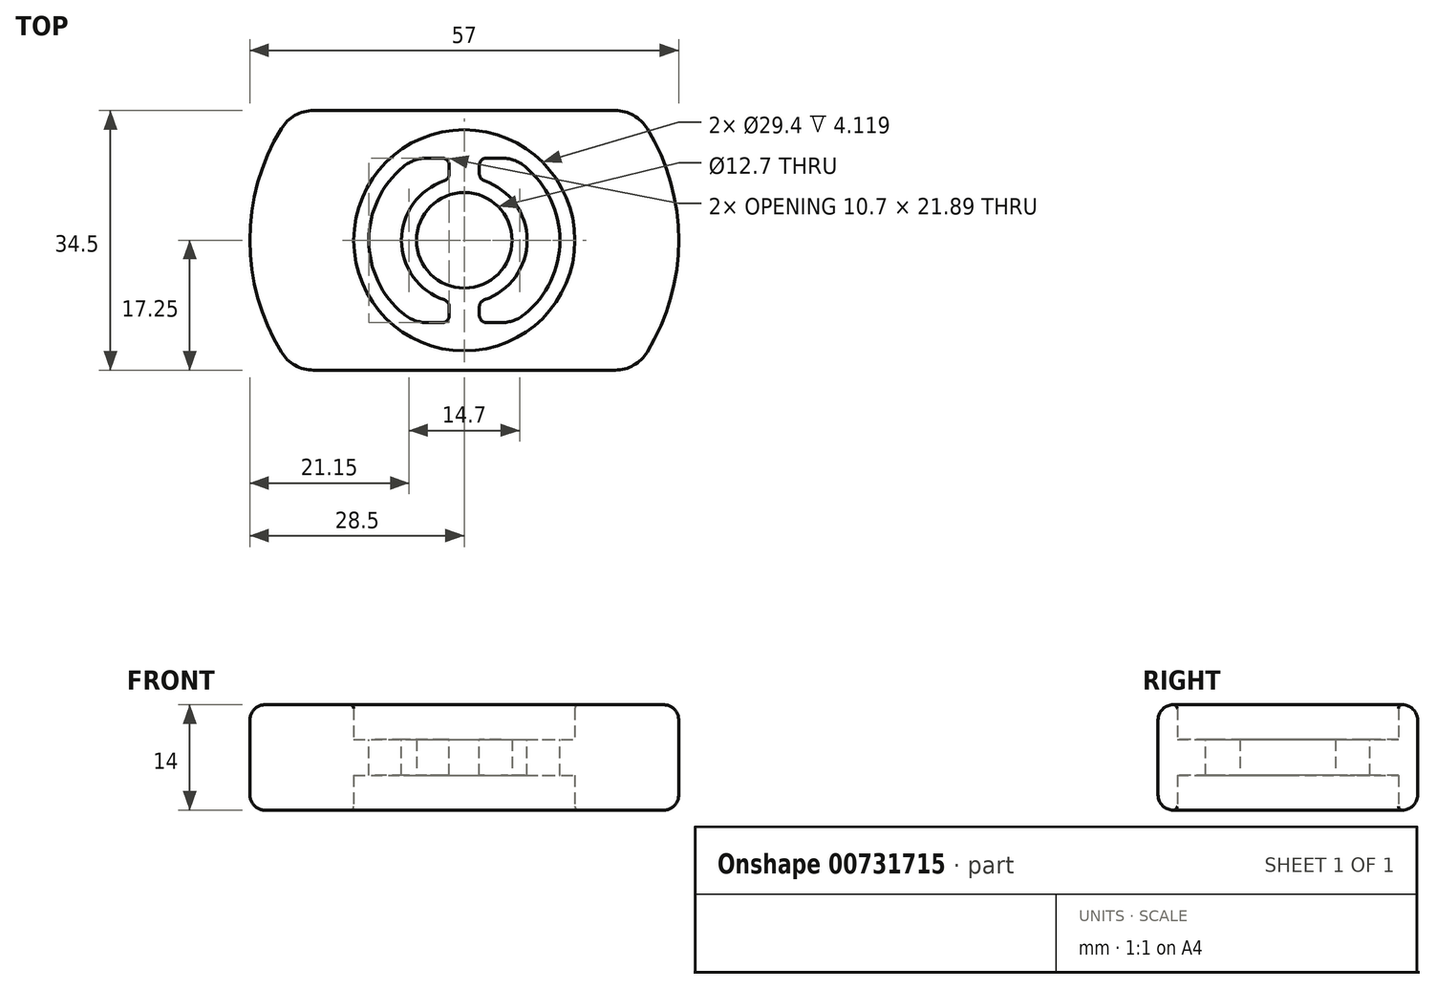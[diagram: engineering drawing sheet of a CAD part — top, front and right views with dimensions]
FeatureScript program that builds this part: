
annotation { "Feature Type Name" : "Feature", "Feature Type Description" : "" }
export const myFeature = defineFeature(function(context is Context, id is Id, definition is map)
    precondition{}
    {
        {
            var Q0;
            Q0=qCreatedBy(makeId("Front.planeOp"),FACE);
            var sketch = newSketch(context, id + "F0", { "sketchPlane" : qUnion([Q0])});
            skLineSegment(sketch, "E0", {"start": v(6.35, 0) * mm, "end": v(6.35, 4.76) * mm});
            skLineSegment(sketch, "E1", {"start": v(0, 6.26) * mm, "end": v(0, 11.13) * mm});
            skLineSegment(sketch, "E2", {"start": v(0, 19.9) * mm, "end": v(12.7, 19.9) * mm});
            skLineSegment(sketch, "E3", {"start": v(6.35, 4.76) * mm, "end": v(12.7, 4.76) * mm});
            skLineSegment(sketch, "E4", {"start": v(6.35, 0) * mm, "end": v(12.7, 0) * mm});
            skLineSegment(sketch, "E5", {"start": v(12.7, 4.76) * mm, "end": v(14.7, 4.76) * mm});
            skLineSegment(sketch, "E6", {"start": v(12.7, 0) * mm, "end": v(14.7, 0) * mm});
            skLineSegment(sketch, "E7", {"start": v(14.7, 4.76) * mm, "end": v(14.7, 6.26) * mm});
            skLineSegment(sketch, "E8", {"start": v(14.7, 0) * mm, "end": v(14.7, -1.5) * mm});
            skLineSegment(sketch, "E9", {"start": v(28.5, 2.38) * mm, "end": v(28.5, -4.62) * mm});
            skLineSegment(sketch, "E10", {"start": v(29.18, -4.62) * mm, "end": v(28.5, -4.62) * mm});
            skPoint(sketch, "E11.start.orphan", {"position": v(29.18, 11.38) * mm});
            skLineSegment(sketch, "E12", {"start": v(28.5, -4.62) * mm, "end": v(24.5, -4.62) * mm});
            skPoint(sketch, "E13.orphan", {"position": v(28.5, 13.95) * mm});
            skLineSegment(sketch, "E14", {"start": v(8.65, 12.63) * mm, "end": v(7.14, 12.63) * mm});
            skLineSegment(sketch, "E15", {"start": v(12.7, 6.26) * mm, "end": v(12.7, 6.26) * mm});
            skPoint(sketch, "E16.orphan", {"position": v(0, 12.63) * mm});
            skLineSegment(sketch, "E17", {"start": v(0, 0) * mm, "end": v(0, 4.76) * mm});
            skPoint(sketch, "E18.start.orphan", {"position": v(6.35, 2.38) * mm});
            skLineSegment(sketch, "E19", {"start": v(28.5, 2.38) * mm, "end": v(28.5, 9.38) * mm});
            skLineSegment(sketch, "E20", {"start": v(28.5, 9.38) * mm, "end": v(24.5, 9.38) * mm});
            skPoint(sketch, "E21.end.orphan", {"position": v(24.5, 11.13) * mm});
            skPoint(sketch, "E22.start.orphan", {"position": v(25.51, 2.38) * mm});
            skLineSegment(sketch, "E23", {"start": v(0, 4.76) * mm, "end": v(0, 6.26) * mm});
            skPoint(sketch, "E24.startSnap0", {"position": v(0, 5.51) * mm});
            skLineSegment(sketch, "E25", {"start": v(8.65, 10.26) * mm, "end": v(7.14, 10.26) * mm});
            skPoint(sketch, "E26.orphan", {"position": v(8.65, 11.13) * mm});
            skPoint(sketch, "E27.start.orphan", {"position": v(8.65, 9.38) * mm});
            skLineSegment(sketch, "E28", {"start": v(12.7, 5.51) * mm, "end": v(0, 5.51) * mm});
            skLineSegment(sketch, "E29", {"start": v(12.7, 5.51) * mm, "end": v(13.7, 5.51) * mm});
            skPoint(sketch, "E29.endSnap0", {"position": v(13.7, 4.76) * mm});
            skLineSegment(sketch, "E30", {"start": v(13.7, 5.51) * mm, "end": v(13.7, 6.26) * mm});
            skLineSegment(sketch, "E31", {"start": v(4.54, 2.38) * mm, "end": v(2.3, 2.38) * mm});
            skLineSegment(sketch, "E32.MirrorCS", {"start": v(12.7, -0.75) * mm, "end": v(0, -0.75) * mm});
            skLineSegment(sketch, "E33", {"start": v(13.7, -1.5) * mm, "end": v(13.7, -0.75) * mm});
            skLineSegment(sketch, "E34", {"start": v(13.7, -0.75) * mm, "end": v(12.7, -0.75) * mm});
            skLineSegment(sketch, "E35", {"start": v(0, -3.93) * mm, "end": v(0, -0.75) * mm});
            skLineSegment(sketch, "E36", {"start": v(14.7, -1.5) * mm, "end": v(14.7, -4.62) * mm});
            skLineSegment(sketch, "E37", {"start": v(14.7, -4.62) * mm, "end": v(24.5, -4.62) * mm});
            skLineSegment(sketch, "E38", {"start": v(24.5, 9.38) * mm, "end": v(14.7, 9.38) * mm});
            skLineSegment(sketch, "E39", {"start": v(14.7, 9.38) * mm, "end": v(14.7, 6.26) * mm});
            skPoint(sketch, "E40.start.orphan", {"position": v(0, 8.7) * mm});
            skLineSegment(sketch, "E41", {"start": v(13.7, 6.26) * mm, "end": v(13.7, 10.26) * mm});
            skLineSegment(sketch, "E42", {"start": v(13.7, 10.26) * mm, "end": v(8.65, 10.26) * mm});
            skPoint(sketch, "E43.MirrorCS.end.orphan", {"position": v(7.14, -5.5) * mm});
            skPoint(sketch, "E43.MirrorCS.start.orphan", {"position": v(0, -3.93) * mm});
            skPoint(sketch, "E44.end.orphan", {"position": v(8.65, -5.5) * mm});
            skLineSegment(sketch, "E45", {"start": v(13.7, -1.5) * mm, "end": v(13.7, -5.5) * mm});
            skLineSegment(sketch, "E46", {"start": v(13.7, -5.5) * mm, "end": v(8.65, -5.5) * mm});
            skLineSegment(sketch, "E47", {"start": v(0, -5.5) * mm, "end": v(0, -3.93) * mm});
            skLineSegment(sketch, "E48", {"start": v(13.7, 10.26) * mm, "end": v(10.5, 10.26) * mm});
            skLineSegment(sketch, "E49", {"start": v(10.5, -5.5) * mm, "end": v(13.7, -5.5) * mm});
            skArc(sketch, "E50", {"start": v(8.65, -5.5) * mm, "mid": v(4.4, -4.33) * mm, "end": v(0, -3.93) * mm});
            skArc(sketch, "E51.MirrorCS", {"start": v(8.65, 10.26) * mm, "mid": v(4.4, 9.1) * mm, "end": v(0, 8.7) * mm});
            skSolve(sketch);
        }
        {
            var Q0;
            Q0=makeQuery(id+"F0.imprint","IMPRINT",FACE,{"disambiguationData":[TD([[makeQuery(id+"F0.imprint","IMPRINT",EDGE,{"derivedFrom":sQuery(id+"F0.wireOp",EDGE,"E0")}),-1.0]])]});
            var Q1;
            Q1=makeQuery(id+"F0.imprint","IMPRINT",FACE,{"disambiguationData":[TD([[makeQuery(id+"F0.imprint","IMPRINT",EDGE,{"derivedFrom":sQuery(id+"F0.wireOp",EDGE,"E32.MirrorCS")}),1.0]])]});
            var Q2;
            {var subQ0=sQuery(id+"F0.wireOp",EDGE,"E28");Q2=makeQuery(id+"F0.imprint","IMPRINT",FACE,{"disambiguationData":[TD([[makeQuery(id+"F0.imprint","IMPRINT",EDGE,{"derivedFrom":subQ0}),-1.0]])]});}
            var Q3;
            Q3=sQuery(id+"F0.wireOp",EDGE,"E17");
            revolve(context, id + "F1", {"surfaceOperationType" : NewSurfaceOperationType.NEW, "entities" : qUnion([Q0, Q1, Q2]), "axis" : qUnion([Q3]), "revolveType" : RevolveType.FULL});
        }
        {
            var Q0;
            Q0=qCreatedBy(makeId("Top.planeOp"),FACE);
            var sketch = newSketch(context, id + "F2", { "sketchPlane" : qUnion([Q0])});
            skPoint(sketch, "E52.middle", {"position": v(0, 0) * mm});
            skLineSegment(sketch, "E53", {"start": v(0, 0) * mm, "end": v(45.47, 0) * mm});
            skPoint(sketch, "E53.endSnap0", {"position": v(17.25, 0) * mm});
            skLineSegment(sketch, "E54", {"start": v(45.47, 0) * mm, "end": v(-32.67, 0) * mm});
            skPoint(sketch, "E55.center.orphan", {"position": v(0, 49.14) * mm});
            skPoint(sketch, "E56.orphan", {"position": v(17.25, 17.25) * mm});
            skPoint(sketch, "E57.orphan", {"position": v(-17.25, 17.25) * mm});
            skPoint(sketch, "E52.top.start.orphan", {"position": v(17.25, -17.25) * mm});
            skPoint(sketch, "E52.right.end.orphan", {"position": v(-17.25, -17.25) * mm});
            skLineSegment(sketch, "E58.bottom", {"start": v(17.25, -17.25) * mm, "end": v(-17.25, -17.25) * mm});
            skLineSegment(sketch, "E58.top", {"start": v(17.25, 17.25) * mm, "end": v(-17.25, 17.25) * mm});
            skLineSegment(sketch, "E58.left", {"start": v(17.25, -17.25) * mm, "end": v(17.25, 17.25) * mm});
            skLineSegment(sketch, "E58.right", {"start": v(-17.25, -17.25) * mm, "end": v(-17.25, 17.25) * mm});
            skLineSegment(sketch, "E59.bottom", {"start": v(-17.25, -17.25) * mm, "end": v(17.25, -17.25) * mm});
            skLineSegment(sketch, "E60.bottom", {"start": v(-17.25, 17.25) * mm, "end": v(17.25, 17.25) * mm});
            skPoint(sketch, "E60.left.start.orphan", {"position": v(-44.41, 17.25) * mm});
            skPoint(sketch, "E61.orphan", {"position": v(-43.8, -17.25) * mm});
            skLineSegment(sketch, "E62.bottom", {"start": v(-37.17, 17.25) * mm, "end": v(41.6, 17.25) * mm});
            skLineSegment(sketch, "E62.top", {"start": v(-37.17, 42.12) * mm, "end": v(41.6, 42.12) * mm});
            skLineSegment(sketch, "E62.left", {"start": v(-37.17, 17.25) * mm, "end": v(-37.17, 42.12) * mm});
            skLineSegment(sketch, "E62.right", {"start": v(41.6, 17.25) * mm, "end": v(41.6, 42.12) * mm});
            skLineSegment(sketch, "E63.bottom", {"start": v(43.46, -17.25) * mm, "end": v(-37, -17.25) * mm});
            skLineSegment(sketch, "E63.top", {"start": v(43.46, -42.73) * mm, "end": v(-37, -42.73) * mm});
            skLineSegment(sketch, "E63.left", {"start": v(43.46, -17.25) * mm, "end": v(43.46, -42.73) * mm});
            skLineSegment(sketch, "E63.right", {"start": v(-37, -17.25) * mm, "end": v(-37, -42.73) * mm});
            skSolve(sketch);
        }
        {
            var Q0;
            Q0=makeQuery(id+"F2.imprint","IMPRINT",FACE,{"disambiguationData":[TD([[makeQuery(id+"F2.imprint","IMPRINT",EDGE,{"derivedFrom":sQuery(id+"F2.wireOp",EDGE,"E63.top")}),-1.0]])]});
            var Q1;
            Q1=makeQuery(id+"F2.imprint","IMPRINT",FACE,{"disambiguationData":[TD([[makeQuery(id+"F2.imprint","IMPRINT",EDGE,{"derivedFrom":sQuery(id+"F2.wireOp",EDGE,"E62.top")}),-1.0]])]});
            extrude(context, id + "F3", {"entities" : qUnion([Q0, Q1]), "operationType" : NewBodyOperationType.REMOVE, "endBound" : BoundingType.SYMMETRIC, "oppositeDirection" : true, "depth" : 25 * mm, "offsetDistance" : 25 * mm});
        }
        {
            var Q0;
            Q0=makeQuery(id+"F1.opRevolve","SWEPT_FACE",FACE,{"disambiguationData":[OSD([sQuery(id+"F0.wireOp",EDGE,"E3"),sQuery(id+"F0.wireOp",EDGE,"E5")])]});
            var sketch = newSketch(context, id + "F4", { "sketchPlane" : qUnion([Q0])});
            skLineSegment(sketch, "E64", {"start": v(0, 6.35) * mm, "end": v(0, 8.35) * mm});
            skLineSegment(sketch, "E65", {"start": v(0, -6.35) * mm, "end": v(0, -13.35) * mm});
            skPoint(sketch, "E65.startSnap0", {"position": v(0, -13.35) * mm});
            skArc(sketch, "E66.0", {"start": v(-6.44, -10.95) * mm, "mid": v(-12.7, 0) * mm, "end": v(-6.44, 10.95) * mm});
            skLineSegment(sketch, "E67.0", {"start": v(-2, -8.1) * mm, "end": v(-2, -10.95) * mm});
            skLineSegment(sketch, "E68.0", {"start": v(-2, 8.1) * mm, "end": v(-2, 10.95) * mm});
            skArc(sketch, "E69.0", {"start": v(-2, 8.1) * mm, "mid": v(-8.35, 0) * mm, "end": v(-2, -8.1) * mm});
            skLineSegment(sketch, "E70", {"start": v(-6.44, 10.95) * mm, "end": v(-2, 10.95) * mm});
            skLineSegment(sketch, "E71", {"start": v(-6.44, -10.95) * mm, "end": v(-2, -10.95) * mm});
            skPoint(sketch, "E71.endSnap0", {"position": v(-2, -9.85) * mm});
            skPoint(sketch, "E72.orphan", {"position": v(0, 13.35) * mm});
            skPoint(sketch, "E73.orphan", {"position": v(-2, -6.35) * mm});
            skPoint(sketch, "E74.orphan", {"position": v(-2, -13.35) * mm});
            skArc(sketch, "E75.MirrorCS", {"start": v(6.44, -10.95) * mm, "mid": v(12.7, 0) * mm, "end": v(6.44, 10.95) * mm});
            skLineSegment(sketch, "E76.MirrorCS", {"start": v(6.44, -10.95) * mm, "end": v(2, -10.95) * mm});
            skArc(sketch, "E77.MirrorCS", {"start": v(2, 8.1) * mm, "mid": v(8.35, 0) * mm, "end": v(2, -8.1) * mm});
            skLineSegment(sketch, "E78.MirrorCS", {"start": v(2, 8.1) * mm, "end": v(2, 10.95) * mm});
            skLineSegment(sketch, "E79.MirrorCS", {"start": v(6.44, 10.95) * mm, "end": v(2, 10.95) * mm});
            skLineSegment(sketch, "E80", {"start": v(2, -10.95) * mm, "end": v(2, -8.1) * mm});
            skSolve(sketch);
        }
        {
            var Q0;
            Q0=qSketchRegion(id+"F4",true);
            extrude(context, id + "F5", {"entities" : qUnion([Q0]), "operationType" : NewBodyOperationType.REMOVE, "oppositeDirection" : true, "depth" : 25 * mm, "offsetDistance" : 25 * mm});
        }
        {
            var Q0;
            Q0=makeQuery(id+"F5.boolean.opBoolean","COPY",EDGE,{"derivedFrom":makeQuery(id+"F5.opExtrude","SWEPT_EDGE",EDGE,{"disambiguationData":[OSD([sQuery(id+"F4.wireOp",EDGE,"E75.MirrorCS"),sQuery(id+"F4.wireOp",EDGE,"E79.MirrorCS")])]})});
            var Q1;
            Q1=makeQuery(id+"F5.boolean.opBoolean","COPY",EDGE,{"derivedFrom":makeQuery(id+"F5.opExtrude","SWEPT_EDGE",EDGE,{"disambiguationData":[OSD([sQuery(id+"F4.wireOp",EDGE,"E66.0"),sQuery(id+"F4.wireOp",EDGE,"E70")])]})});
            var Q2;
            Q2=makeQuery(id+"F5.boolean.opBoolean","COPY",EDGE,{"derivedFrom":makeQuery(id+"F5.opExtrude","SWEPT_EDGE",EDGE,{"disambiguationData":[OSD([sQuery(id+"F4.wireOp",EDGE,"E66.0"),sQuery(id+"F4.wireOp",EDGE,"E71")])]})});
            var Q3;
            Q3=makeQuery(id+"F5.boolean.opBoolean","COPY",EDGE,{"derivedFrom":makeQuery(id+"F5.opExtrude","SWEPT_EDGE",EDGE,{"disambiguationData":[OSD([sQuery(id+"F4.wireOp",EDGE,"E75.MirrorCS"),sQuery(id+"F4.wireOp",EDGE,"E76.MirrorCS")])]})});
            fillet(context, id + "F6", {"entities" : qUnion([Q0, Q1, Q2, Q3]), "radius" : 5 * mm, "tangentPropagation" : true, "allowEdgeOverflow" : false});
        }
        {
            var Q0;
            Q0=makeQuery(id+"F5.boolean.opBoolean","COPY",EDGE,{"derivedFrom":makeQuery(id+"F5.opExtrude","SWEPT_EDGE",EDGE,{"disambiguationData":[OSD([sQuery(id+"F4.wireOp",EDGE,"E68.0"),sQuery(id+"F4.wireOp",EDGE,"E70")])]})});
            var Q1;
            Q1=makeQuery(id+"F5.boolean.opBoolean","COPY",EDGE,{"derivedFrom":makeQuery(id+"F5.opExtrude","SWEPT_EDGE",EDGE,{"disambiguationData":[OSD([sQuery(id+"F4.wireOp",EDGE,"E77.MirrorCS"),sQuery(id+"F4.wireOp",EDGE,"E78.MirrorCS")])]})});
            var Q2;
            Q2=makeQuery(id+"F5.boolean.opBoolean","COPY",EDGE,{"derivedFrom":makeQuery(id+"F5.opExtrude","SWEPT_EDGE",EDGE,{"disambiguationData":[OSD([sQuery(id+"F4.wireOp",EDGE,"E76.MirrorCS"),sQuery(id+"F4.wireOp",EDGE,"E80")])]})});
            var Q3;
            Q3=makeQuery(id+"F5.boolean.opBoolean","COPY",EDGE,{"derivedFrom":makeQuery(id+"F5.opExtrude","SWEPT_EDGE",EDGE,{"disambiguationData":[OSD([sQuery(id+"F4.wireOp",EDGE,"E68.0"),sQuery(id+"F4.wireOp",EDGE,"E69.0")])]})});
            var Q4;
            Q4=makeQuery(id+"F5.boolean.opBoolean","COPY",EDGE,{"derivedFrom":makeQuery(id+"F5.opExtrude","SWEPT_EDGE",EDGE,{"disambiguationData":[OSD([sQuery(id+"F4.wireOp",EDGE,"E78.MirrorCS"),sQuery(id+"F4.wireOp",EDGE,"E79.MirrorCS")])]})});
            var Q5;
            Q5=makeQuery(id+"F5.boolean.opBoolean","COPY",EDGE,{"derivedFrom":makeQuery(id+"F5.opExtrude","SWEPT_EDGE",EDGE,{"disambiguationData":[OSD([sQuery(id+"F4.wireOp",EDGE,"E77.MirrorCS"),sQuery(id+"F4.wireOp",EDGE,"E80")])]})});
            var Q6;
            Q6=makeQuery(id+"F5.boolean.opBoolean","COPY",EDGE,{"derivedFrom":makeQuery(id+"F5.opExtrude","SWEPT_EDGE",EDGE,{"disambiguationData":[OSD([sQuery(id+"F4.wireOp",EDGE,"E67.0"),sQuery(id+"F4.wireOp",EDGE,"E71")])]})});
            var Q7;
            Q7=makeQuery(id+"F5.boolean.opBoolean","COPY",EDGE,{"derivedFrom":makeQuery(id+"F5.opExtrude","SWEPT_EDGE",EDGE,{"disambiguationData":[OSD([sQuery(id+"F4.wireOp",EDGE,"E67.0"),sQuery(id+"F4.wireOp",EDGE,"E69.0")])]})});
            fillet(context, id + "F7", {"entities" : qUnion([Q0, Q1, Q2, Q3, Q4, Q5, Q6, Q7]), "radius" : 1 * mm, "tangentPropagation" : true, "allowEdgeOverflow" : false});
        }
        {
            var Q0;
            Q0=makeQuery(id+"F3.boolean.opBoolean","INTERSECT",EDGE,{"disambiguationData":[OD(1.0)],"derivedFrom":[makeQuery(id+"F1.opRevolve","SWEPT_FACE",FACE,{"disambiguationData":[OSD([sQuery(id+"F0.wireOp",EDGE,"E9"),sQuery(id+"F0.wireOp",EDGE,"E19")])]}),makeQuery(id+"F3.opExtrude","SWEPT_FACE",FACE,{"disambiguationData":[OSD([sQuery(id+"F2.wireOp",EDGE,"E63.bottom")])]})]});
            var Q1;
            Q1=makeQuery(id+"F3.boolean.opBoolean","INTERSECT",EDGE,{"disambiguationData":[OD(0.0)],"derivedFrom":[makeQuery(id+"F1.opRevolve","SWEPT_FACE",FACE,{"disambiguationData":[OSD([sQuery(id+"F0.wireOp",EDGE,"E9"),sQuery(id+"F0.wireOp",EDGE,"E19")])]}),makeQuery(id+"F3.opExtrude","SWEPT_FACE",FACE,{"disambiguationData":[OSD([sQuery(id+"F2.wireOp",EDGE,"E63.bottom")])]})]});
            var Q2;
            Q2=makeQuery(id+"F3.boolean.opBoolean","INTERSECT",EDGE,{"disambiguationData":[OD(0.0)],"derivedFrom":[makeQuery(id+"F1.opRevolve","SWEPT_FACE",FACE,{"disambiguationData":[OSD([sQuery(id+"F0.wireOp",EDGE,"E9"),sQuery(id+"F0.wireOp",EDGE,"E19")])]}),makeQuery(id+"F3.opExtrude","SWEPT_FACE",FACE,{"disambiguationData":[OSD([sQuery(id+"F2.wireOp",EDGE,"E62.bottom")])]})]});
            var Q3;
            Q3=makeQuery(id+"F3.boolean.opBoolean","INTERSECT",EDGE,{"disambiguationData":[OD(1.0)],"derivedFrom":[makeQuery(id+"F1.opRevolve","SWEPT_FACE",FACE,{"disambiguationData":[OSD([sQuery(id+"F0.wireOp",EDGE,"E9"),sQuery(id+"F0.wireOp",EDGE,"E19")])]}),makeQuery(id+"F3.opExtrude","SWEPT_FACE",FACE,{"disambiguationData":[OSD([sQuery(id+"F2.wireOp",EDGE,"E62.bottom")])]})]});
            fillet(context, id + "F8", {"entities" : qUnion([Q0, Q1, Q2, Q3]), "radius" : 5 * mm, "tangentPropagation" : true, "allowEdgeOverflow" : false});
        }
        {
            var Q0;
            Q0=makeQuery(id+"F3.boolean.opBoolean","INTERSECT",EDGE,{"derivedFrom":[makeQuery(id+"F1.opRevolve","SWEPT_FACE",FACE,{"disambiguationData":[OSD([sQuery(id+"F0.wireOp",EDGE,"E20"),sQuery(id+"F0.wireOp",EDGE,"E38")])]}),makeQuery(id+"F3.opExtrude","SWEPT_FACE",FACE,{"disambiguationData":[OSD([sQuery(id+"F2.wireOp",EDGE,"E62.bottom")])]})]});
            var Q1;
            Q1=makeQuery(id+"F3.boolean.opBoolean","INTERSECT",EDGE,{"derivedFrom":[makeQuery(id+"F1.opRevolve","SWEPT_FACE",FACE,{"disambiguationData":[OSD([sQuery(id+"F0.wireOp",EDGE,"E12"),sQuery(id+"F0.wireOp",EDGE,"E37")])]}),makeQuery(id+"F3.opExtrude","SWEPT_FACE",FACE,{"disambiguationData":[OSD([sQuery(id+"F2.wireOp",EDGE,"E62.bottom")])]})]});
            fillet(context, id + "F9", {"entities" : qUnion([Q0, Q1]), "radius" : 2 * mm, "tangentPropagation" : true, "allowEdgeOverflow" : false});
        }
        {
            var Q0;
            Q0=makeQuery(id+"F1.opRevolve","SWEPT_EDGE",EDGE,{"disambiguationData":[OSD([sQuery(id+"F0.wireOp",EDGE,"E41"),sQuery(id+"F0.wireOp",EDGE,"E48")])]});
            fillet(context, id + "F10", {"entities" : qUnion([Q0]), "radius" : 1 * mm, "tangentPropagation" : true, "allowEdgeOverflow" : false});
        }
        {
            var Q0;
            Q0=makeQuery(id+"F1.opRevolve","SWEPT_EDGE",EDGE,{"disambiguationData":[OSD([sQuery(id+"F0.wireOp",EDGE,"E38"),sQuery(id+"F0.wireOp",EDGE,"E39")])]});
            fillet(context, id + "F11", {"entities" : qUnion([Q0]), "radius" : .5 * mm, "tangentPropagation" : true, "allowEdgeOverflow" : false});
        }
        {
            var Q0;
            Q0=makeQuery(id+"F1.opRevolve","SWEPT_EDGE",EDGE,{"disambiguationData":[OSD([sQuery(id+"F0.wireOp",EDGE,"E45"),sQuery(id+"F0.wireOp",EDGE,"E49")])]});
            fillet(context, id + "F12", {"entities" : qUnion([Q0]), "radius" : 1 * mm, "tangentPropagation" : true, "allowEdgeOverflow" : false});
        }
        {
            var Q0;
            Q0=makeQuery(id+"F1.opRevolve","SWEPT_EDGE",EDGE,{"disambiguationData":[OSD([sQuery(id+"F0.wireOp",EDGE,"E36"),sQuery(id+"F0.wireOp",EDGE,"E37")])]});
            fillet(context, id + "F13", {"entities" : qUnion([Q0]), "radius" : .5 * mm, "tangentPropagation" : true, "allowEdgeOverflow" : false});
        }
        {
            var Q0;
            Q0=makeQuery(id+"F1.opRevolve","SWEPT_BODY",BODY,{"disambiguationData":[OSD([sQuery(id+"F0.wireOp",EDGE,"E1"),sQuery(id+"F0.wireOp",EDGE,"E23"),sQuery(id+"F0.wireOp",EDGE,"E28"),sQuery(id+"F0.wireOp",EDGE,"E29"),sQuery(id+"F0.wireOp",EDGE,"E30"),sQuery(id+"F0.wireOp",EDGE,"E41"),sQuery(id+"F0.wireOp",EDGE,"E42"),sQuery(id+"F0.wireOp",EDGE,"E48"),sQuery(id+"F0.wireOp",EDGE,"E51.MirrorCS")])]});
            deleteBodies(context, id + "F14", {"entities" : qUnion([Q0])});
        }
        {
            var Q0;
            Q0=makeQuery(id+"F1.opRevolve","SWEPT_BODY",BODY,{"disambiguationData":[OSD([sQuery(id+"F0.wireOp",EDGE,"E32.MirrorCS"),sQuery(id+"F0.wireOp",EDGE,"E33"),sQuery(id+"F0.wireOp",EDGE,"E34"),sQuery(id+"F0.wireOp",EDGE,"E35"),sQuery(id+"F0.wireOp",EDGE,"E45"),sQuery(id+"F0.wireOp",EDGE,"E46"),sQuery(id+"F0.wireOp",EDGE,"E49"),sQuery(id+"F0.wireOp",EDGE,"E50")])]});
            deleteBodies(context, id + "F15", {"entities" : qUnion([Q0])});
        }
    });
